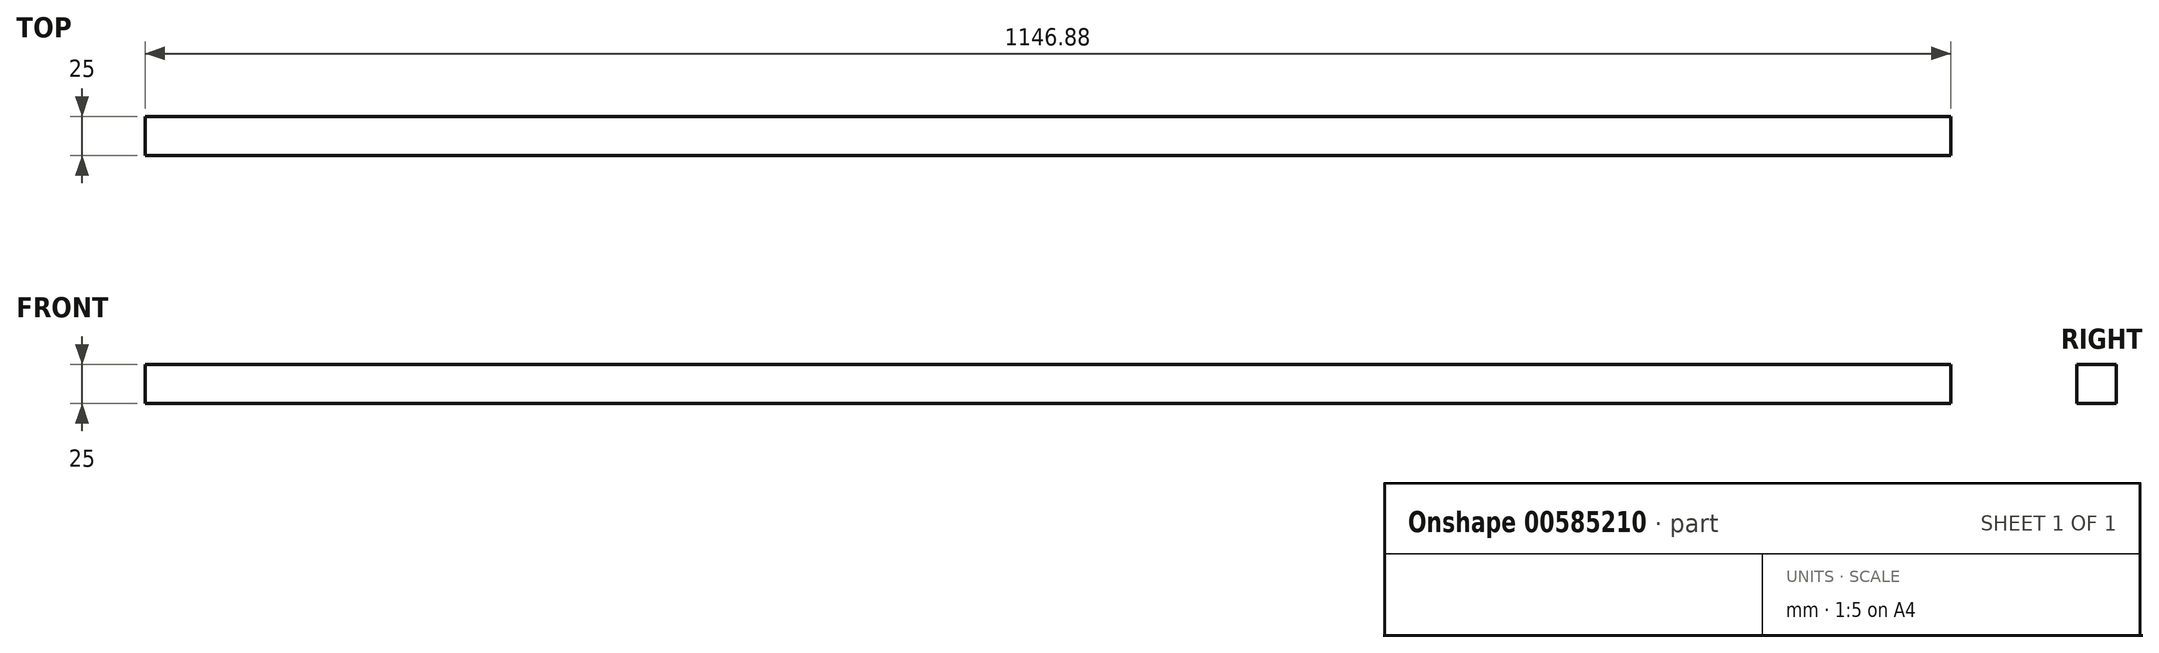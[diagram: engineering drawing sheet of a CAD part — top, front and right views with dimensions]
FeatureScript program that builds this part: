
annotation { "Feature Type Name" : "Feature", "Feature Type Description" : "" }
export const myFeature = defineFeature(function(context is Context, id is Id, definition is map)
    precondition{}
    {
        {
            var Q0;
            Q0=qCreatedBy(makeId("Front.planeOp"),FACE);
            var sketch = newSketch(context, id + "F0", { "sketchPlane" : qUnion([Q0])});
            skLineSegment(sketch, "E0.bottom", {"start": v(0, 0) * mm, "end": v(1146.88, 0) * mm});
            skLineSegment(sketch, "E0.top", {"start": v(0, 25) * mm, "end": v(1146.88, 25) * mm});
            skLineSegment(sketch, "E0.left", {"start": v(0, 0) * mm, "end": v(0, 25) * mm});
            skLineSegment(sketch, "E0.right", {"start": v(1146.88, 0) * mm, "end": v(1146.88, 25) * mm});
            skSolve(sketch);
        }
        {
            var Q0;
            Q0=makeQuery(id+"F0.imprint","IMPRINT",FACE,{"disambiguationData":[TD([[makeQuery(id+"F0.imprint","IMPRINT",EDGE,{"derivedFrom":sQuery(id+"F0.wireOp",EDGE,"E0.bottom")}),1.0]])]});
            extrude(context, id + "F1", {"entities" : qUnion([Q0]), "endBound" : BoundingType.SYMMETRIC, "depth" : 25 * mm, "offsetDistance" : 25 * mm});
        }
    });
